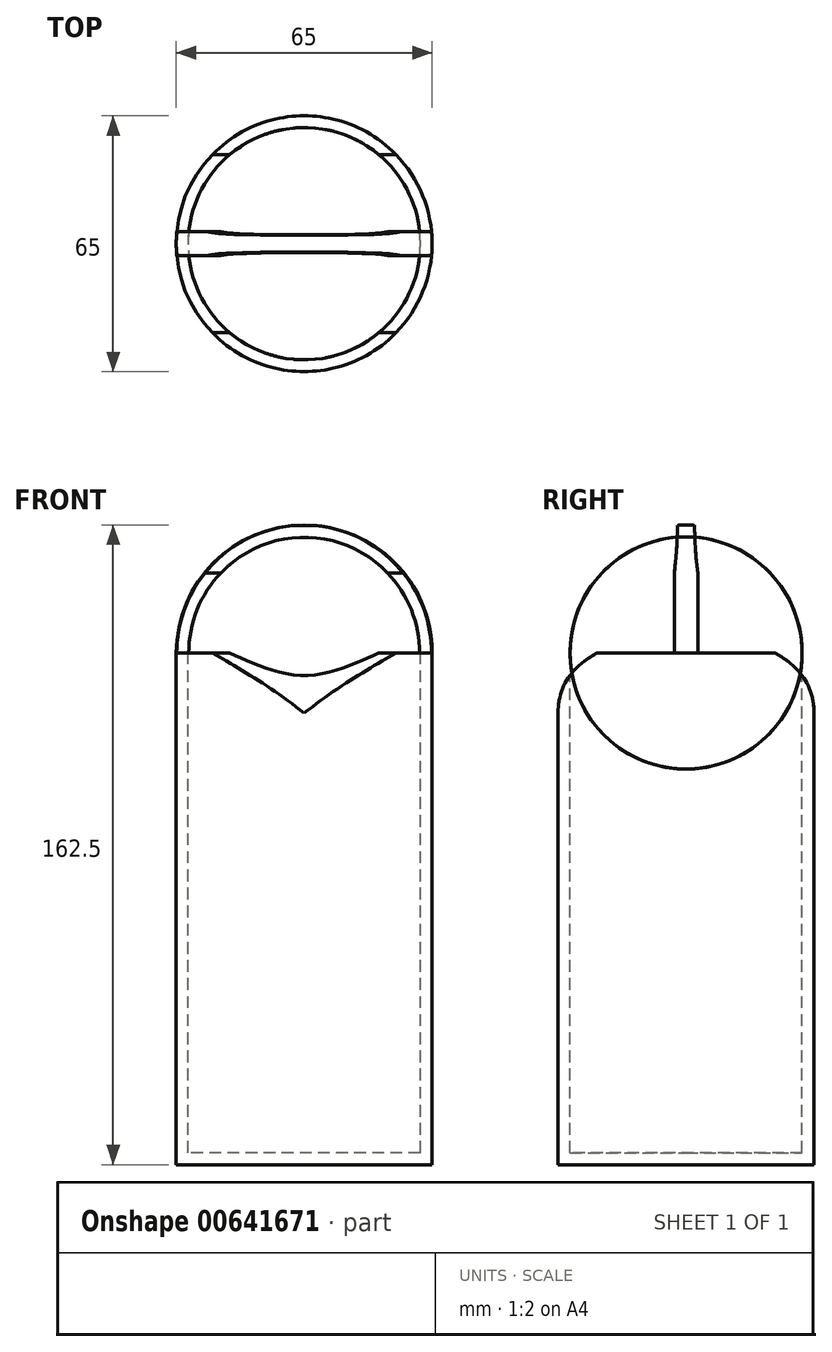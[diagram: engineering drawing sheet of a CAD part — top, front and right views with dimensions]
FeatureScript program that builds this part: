
annotation { "Feature Type Name" : "Feature", "Feature Type Description" : "" }
export const myFeature = defineFeature(function(context is Context, id is Id, definition is map)
    precondition{}
    {
        {
            var Q0;
            Q0=qCreatedBy(makeId("Front.planeOp"),FACE);
            var sketch = newSketch(context, id + "F0", { "sketchPlane" : qUnion([Q0])});
            skArc(sketch, "E0", {"start": v(0, 96) * mm, "mid": v(-22.98, 86.48) * mm, "end": v(-32.5, 63.5) * mm});
            skLineSegment(sketch, "E1", {"start": v(-32.5, 63.5) * mm, "end": v(-32.5, -66.5) * mm});
            skLineSegment(sketch, "E2", {"start": v(-32.5, -66.5) * mm, "end": v(0, -66.5) * mm});
            skArc(sketch, "E3.0", {"start": v(0, 93) * mm, "mid": v(-20.86, 84.36) * mm, "end": v(-29.5, 63.5) * mm});
            skLineSegment(sketch, "E3.2", {"start": v(-29.5, -63.5) * mm, "end": v(0, -63.5) * mm});
            skLineSegment(sketch, "E3.3", {"start": v(-29.5, 63.5) * mm, "end": v(-29.5, -63.5) * mm});
            skPoint(sketch, "E4", {"position": v(-29.5, 0) * mm});
            skLineSegment(sketch, "E5", {"start": v(0, 96) * mm, "end": v(0, -66.5) * mm});
            skPoint(sketch, "E6.orphan", {"position": v(0, -63.5) * mm});
            skLineSegment(sketch, "E7", {"start": v(0, 96) * mm, "end": v(0, 93) * mm});
            skLineSegment(sketch, "E8", {"start": v(0, -66.5) * mm, "end": v(0, -63.5) * mm});
            skLineSegment(sketch, "E9", {"start": v(-29.5, 63.5) * mm, "end": v(-32.5, 63.5) * mm});
            skSolve(sketch);
        }
        {
            var Q0;
            Q0=makeQuery(id+"F0.imprint","IMPRINT",FACE,{"disambiguationData":[TD([[makeQuery(id+"F0.imprint","IMPRINT",EDGE,{"derivedFrom":sQuery(id+"F0.wireOp",EDGE,"E0")}),1.0]])]});
            var Q1;
            Q1=sQuery(id+"F0.wireOp",EDGE,"E5");
            revolve(context, id + "F1", {"entities" : qUnion([Q0]), "axis" : qUnion([Q1]), "revolveType" : RevolveType.FULL});
        }
        {
            var Q0;
            Q0=qCreatedBy(makeId("Front.planeOp"),FACE);
            var sketch = newSketch(context, id + "F2", { "sketchPlane" : qUnion([Q0])});
            skLineSegment(sketch, "E10.bottom", {"start": v(-44.63, 113.28) * mm, "end": v(47.26, 113.28) * mm});
            skLineSegment(sketch, "E10.top", {"start": v(-44.63, 60.25) * mm, "end": v(47.26, 60.25) * mm});
            skLineSegment(sketch, "E10.left", {"start": v(-44.63, 113.28) * mm, "end": v(-44.63, 60.25) * mm});
            skLineSegment(sketch, "E10.right", {"start": v(47.26, 113.28) * mm, "end": v(47.26, 60.25) * mm});
            skSolve(sketch);
        }
        {
            var Q0;
            Q0=makeQuery(id+"F0.imprint","IMPRINT",FACE,{"disambiguationData":[TD([[makeQuery(id+"F0.imprint","IMPRINT",EDGE,{"derivedFrom":sQuery(id+"F0.wireOp",EDGE,"E1")}),1.0]])]});
            var Q1;
            Q1=sQuery(id+"F0.wireOp",EDGE,"E5");
            revolve(context, id + "F3", {"entities" : qUnion([Q0]), "axis" : qUnion([Q1]), "revolveType" : RevolveType.FULL});
        }
        {
            var Q0;
            Q0=qCreatedBy(makeId("Right.planeOp"),FACE);
            var sketch = newSketch(context, id + "F4", { "sketchPlane" : qUnion([Q0])});
            skFitSpline(sketch, "E11", {"points": [v(-2.1, 101.21) * mm, v(-13.79, 67.76) * mm, v(-32.5, 48.2) * mm], "startDerivative": vector(0, -141.38) * mm, "endDerivative": vector(0, -80.72) * mm});
            skLineSegment(sketch, "E12.0", {"start": v(-32.5, 63.5) * mm, "end": v(32.5, 63.5) * mm});
            skLineSegment(sketch, "E13", {"start": v(-32.5, 48.2) * mm, "end": v(-40.24, 48.2) * mm});
            skLineSegment(sketch, "E14", {"start": v(-40.24, 48.2) * mm, "end": v(-40.24, 101.21) * mm});
            skLineSegment(sketch, "E15", {"start": v(-40.24, 101.21) * mm, "end": v(-2.1, 101.21) * mm});
            skFitSpline(sketch, "E16.MirrorCS", {"points": [v(2.1, 101.21) * mm, v(13.79, 67.76) * mm, v(32.5, 48.2) * mm], "startDerivative": vector(0, -141.38) * mm, "endDerivative": vector(0, -80.72) * mm});
            skLineSegment(sketch, "E17.MirrorCS", {"start": v(32.5, 48.2) * mm, "end": v(40.24, 48.2) * mm});
            skLineSegment(sketch, "E18.MirrorCS", {"start": v(40.24, 48.2) * mm, "end": v(40.24, 101.21) * mm});
            skLineSegment(sketch, "E19.MirrorCS", {"start": v(40.24, 101.21) * mm, "end": v(2.1, 101.21) * mm});
            skSolve(sketch);
        }
        {
            var Q0;
            {var subQ0=sQuery(id+"F4.wireOp",EDGE,"E13");Q0=makeQuery(id+"F4.imprint","IMPRINT",FACE,{"disambiguationData":[TD([[makeQuery(id+"F4.imprint","IMPRINT",EDGE,{"derivedFrom":subQ0}),-1.0]])]});}
            var Q1;
            {var subQ0=sQuery(id+"F4.wireOp",EDGE,"E17.MirrorCS");Q1=makeQuery(id+"F4.imprint","IMPRINT",FACE,{"disambiguationData":[TD([[makeQuery(id+"F4.imprint","IMPRINT",EDGE,{"derivedFrom":subQ0}),1.0]])]});}
            extrude(context, id + "F5", {"entities" : qUnion([Q0, Q1]), "operationType" : NewBodyOperationType.REMOVE, "endBound" : BoundingType.THROUGH_ALL, "oppositeDirection" : true, "depth" : 25 * mm, "offsetDistance" : 25 * mm, "hasSecondDirection" : true, "secondDirectionBound" : SecondDirectionBoundingType.THROUGH_ALL, "secondDirectionOppositeDirection" : false, "secondDirectionDepth" : 25 * mm});
        }
        {
            var Q0;
            Q0=makeQuery(id+"F2.imprint","IMPRINT",FACE,{"disambiguationData":[TD([[makeQuery(id+"F2.imprint","IMPRINT",EDGE,{"derivedFrom":sQuery(id+"F2.wireOp",EDGE,"E10.bottom")}),-1.0]])]});
            extrude(context, id + "F6", {"entities" : qUnion([Q0]), "endBound" : BoundingType.SYMMETRIC, "depth" : 6 * mm, "offsetDistance" : 25 * mm});
        }
        {
            var Q0;
            Q0=makeQuery(id+"F6.opExtrude","SWEPT_BODY",BODY,{"disambiguationData":[OSD([sQuery(id+"F2.wireOp",EDGE,"E10.bottom"),sQuery(id+"F2.wireOp",EDGE,"E10.top"),sQuery(id+"F2.wireOp",EDGE,"E10.left"),sQuery(id+"F2.wireOp",EDGE,"E10.right")])]});
            var Q1;
            Q1=makeQuery(id+"F1.opRevolve","SWEPT_BODY",BODY,{"disambiguationData":[OSD([sQuery(id+"F0.wireOp",EDGE,"E0"),sQuery(id+"F0.wireOp",EDGE,"E1"),sQuery(id+"F0.wireOp",EDGE,"E2"),sQuery(id+"F0.wireOp",EDGE,"E3.0"),sQuery(id+"F0.wireOp",EDGE,"E3.2"),sQuery(id+"F0.wireOp",EDGE,"E3.3"),sQuery(id+"F0.wireOp",EDGE,"E7"),sQuery(id+"F0.wireOp",EDGE,"E8")])]});
            booleanBodies(context, id + "F7", {"operationType" : BooleanOperationType.INTERSECTION, "tools" : qUnion([Q0, Q1])});
        }
    });
